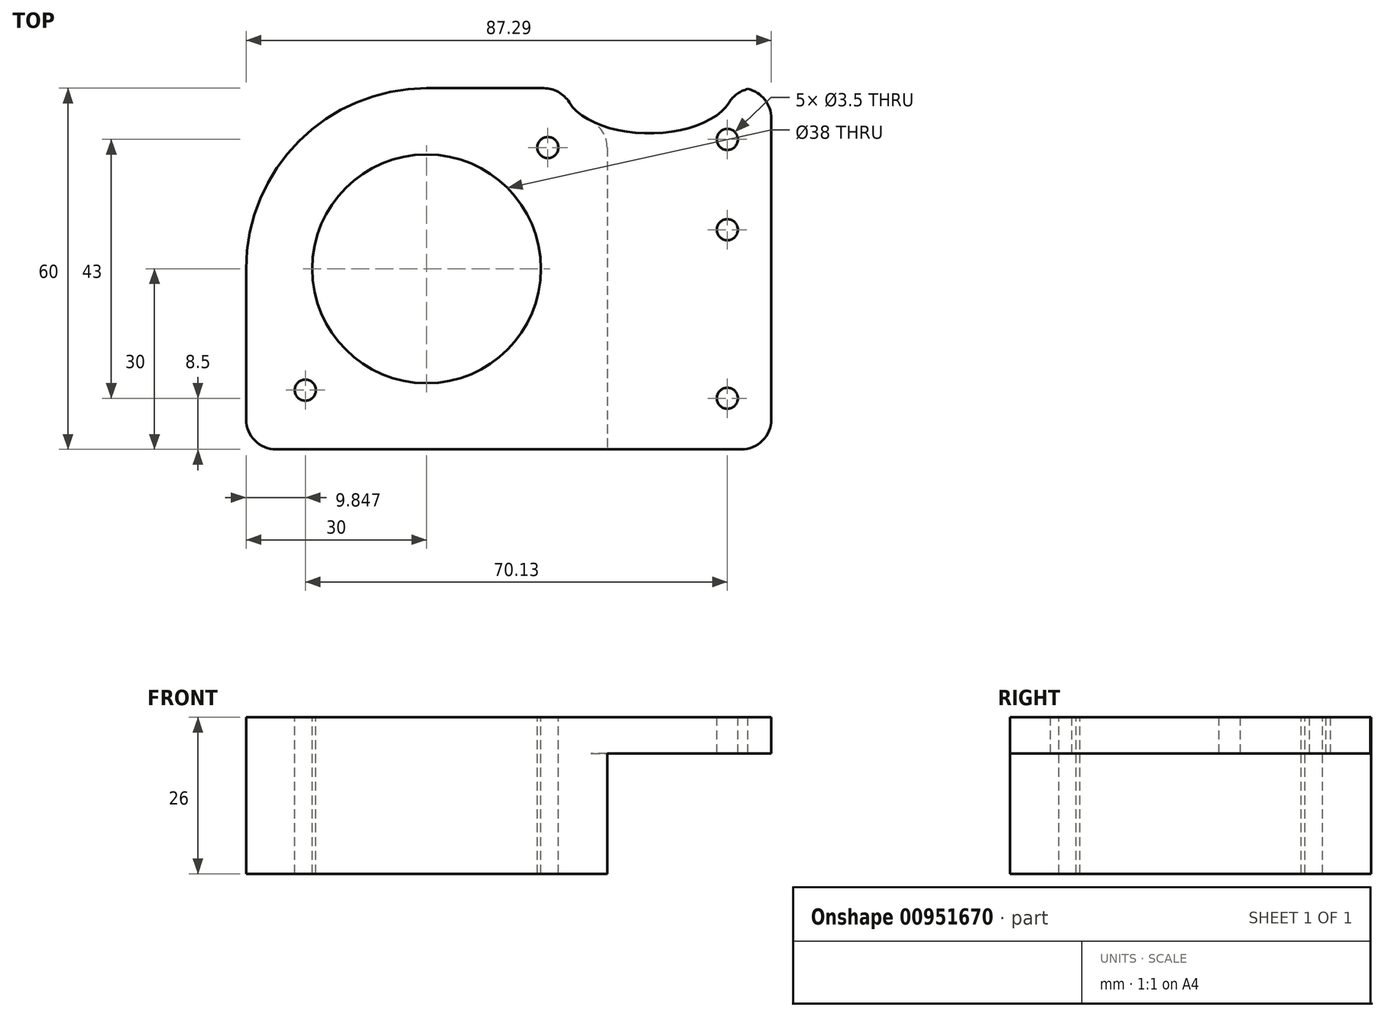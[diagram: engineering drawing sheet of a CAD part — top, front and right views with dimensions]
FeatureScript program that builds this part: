
annotation { "Feature Type Name" : "Feature", "Feature Type Description" : "" }
export const myFeature = defineFeature(function(context is Context, id is Id, definition is map)
    precondition{}
    {
        {
            var Q0;
            Q0=qCreatedBy(makeId("Top.planeOp"),FACE);
            var sketch = newSketch(context, id + "F0", { "sketchPlane" : qUnion([Q0])});
            skLineSegment(sketch, "E0.bottom", {"start": v(-68.25, 37.5) * mm, "end": v(68.25, 37.5) * mm});
            skLineSegment(sketch, "E0.top", {"start": v(-68.25, -37.5) * mm, "end": v(68.25, -37.5) * mm});
            skLineSegment(sketch, "E0.left", {"start": v(-68.25, 37.5) * mm, "end": v(-68.25, -37.5) * mm});
            skLineSegment(sketch, "E0.right", {"start": v(68.25, 37.5) * mm, "end": v(68.25, -37.5) * mm});
            skPoint(sketch, "E0.middle", {"position": v(0, 0) * mm});
            skCircle(sketch, "E1", {"center": v(-68.25, 37.5) * mm, "radius": 2.75 * mm});
            skCircle(sketch, "E2", {"center": v(68.25, 37.5) * mm, "radius": 2.75 * mm});
            skCircle(sketch, "E3", {"center": v(68.25, -37.5) * mm, "radius": 2.75 * mm});
            skCircle(sketch, "E4", {"center": v(-68.25, -37.5) * mm, "radius": 2.75 * mm});
            skEllipse(sketch, "E5", {"center": v(0, 37.5) * mm, "majorRadius": 6 * mm, "minorRadius": 2.75 * mm, "majorAxis": v(0, 1)});
            skEllipse(sketch, "E6", {"center": v(0, -37.5) * mm, "majorRadius": 6 * mm, "minorRadius": 2.75 * mm, "majorAxis": v(0, 1)});
            skLineSegment(sketch, "E7.bottom", {"start": v(-68.25, 37.5) * mm, "end": v(-75.25, 37.5) * mm});
            skLineSegment(sketch, "E7.top", {"start": v(-68.25, -37.5) * mm, "end": v(-75.25, -37.5) * mm});
            skLineSegment(sketch, "E7.right", {"start": v(-75.25, 37.5) * mm, "end": v(-75.25, -37.5) * mm});
            skLineSegment(sketch, "E8.bottom", {"start": v(-135.25, 37.5) * mm, "end": v(-75.25, 37.5) * mm});
            skLineSegment(sketch, "E8.top", {"start": v(-135.25, -22.5) * mm, "end": v(-75.25, -22.5) * mm});
            skLineSegment(sketch, "E8.left", {"start": v(-135.25, 37.5) * mm, "end": v(-135.25, -22.5) * mm});
            skLineSegment(sketch, "E8.right", {"start": v(-75.25, 30) * mm, "end": v(-75.25, -30) * mm});
            skPoint(sketch, "E8.middle", {"position": v(-75.25, 0) * mm});
            skCircle(sketch, "E9", {"center": v(-85.1, 27.65) * mm, "radius": 1.75 * mm});
            skCircle(sketch, "E10", {"center": v(-125.4, -12.65) * mm, "radius": 1.75 * mm});
            skCircle(sketch, "E11", {"center": v(-105.25, 7.5) * mm, "radius": 19 * mm});
            skCircle(sketch, "E12", {"center": v(-55.27, 29) * mm, "radius": 1.75 * mm});
            skCircle(sketch, "E13", {"center": v(-55.27, -14) * mm, "radius": 1.75 * mm});
            skCircle(sketch, "E14", {"center": v(-55.27, 14) * mm, "radius": 1.75 * mm});
            skEllipse(sketch, "E15", {"center": v(-68.25, 37.5) * mm, "majorRadius": 14 * mm, "minorRadius": 7.5 * mm, "majorAxis": v(-1, 0)});
            skLineSegment(sketch, "E16", {"start": v(-47.96, 37.5) * mm, "end": v(-47.96, -37.5) * mm});
            skLineSegment(sketch, "E17", {"start": v(-75.25, -22.5) * mm, "end": v(-47.96, -22.5) * mm});
            skArc(sketch, "E18", {"start": v(-105.25, 37.5) * mm, "mid": v(-126.46, 28.71) * mm, "end": v(-135.25, 7.5) * mm});
            skSolve(sketch);
        }
        {
            var Q0;
            Q0=makeQuery(id+"F0.imprint","IMPRINT",FACE,{"disambiguationData":[TD([[makeQuery(id+"F0.imprint","IMPRINT",EDGE,{"derivedFrom":sQuery(id+"F0.wireOp",EDGE,"E12")}),-1.0]])]});
            var Q1;
            {var subQ0=sQuery(id+"F0.wireOp",EDGE,"E15");var subQ1=sQuery(id+"F0.wireOp",EDGE,"E0.left");var subQ2=makeQuery(id+"F0.imprint","INTERSECT",VERTEX,{"derivedFrom":[subQ1,subQ0]});Q1=makeQuery(id+"F0.imprint","IMPRINT",FACE,{"disambiguationData":[TD([[makeQuery(id+"F0.imprint","IMPRINT",EDGE,{"disambiguationData":[TD([[subQ2,-1.0]])],"derivedFrom":subQ1}),-1.0]])]});}
            extrude(context, id + "F1", {"entities" : qUnion([Q0, Q1]), "oppositeDirection" : true, "depth" : 6 * mm, "offsetDistance" : 25 * mm});
        }
        {
            var Q0;
            {var subQ0=sQuery(id+"F0.wireOp",EDGE,"E8.top");Q0=makeQuery(id+"F0.imprint","IMPRINT",FACE,{"disambiguationData":[TD([[makeQuery(id+"F0.imprint","IMPRINT",EDGE,{"derivedFrom":subQ0}),1.0]])]});}
            extrude(context, id + "F2", {"entities" : qUnion([Q0]), "operationType" : NewBodyOperationType.ADD, "depth" : -26 * mm, "offsetDistance" : 25 * mm});
        }
        {
            var Q0;
            Q0=makeQuery(id+"F2.opExtrude","SWEPT_EDGE",EDGE,{"disambiguationData":[OSD([sQuery(id+"F0.wireOp",EDGE,"E8.bottom"),sQuery(id+"F0.wireOp",EDGE,"E8.left")])]});
            var Q1;
            Q1=makeQuery(id+"F2.opExtrude","SWEPT_EDGE",EDGE,{"disambiguationData":[OSD([sQuery(id+"F0.wireOp",EDGE,"E8.top"),sQuery(id+"F0.wireOp",EDGE,"E8.left")])]});
            var Q2;
            Q2=makeQuery(id+"F2.opExtrude","SWEPT_EDGE",EDGE,{"disambiguationData":[OSD([sQuery(id+"F0.wireOp",EDGE,"E7.bottom"),sQuery(id+"F0.wireOp",EDGE,"E7.right"),sQuery(id+"F0.wireOp",EDGE,"E8.bottom")])]});
            var Q3;
            {var subQ0=sQuery(id+"F0.wireOp",EDGE,"E8.right");var subQ1=sQuery(id+"F0.wireOp",EDGE,"E8.top");Q3=makeQuery(id+"F2.boolean.opBoolean","SPLIT",EDGE,{"disambiguationData":[topologyDisambiguationEdgeConnected([makeQuery(id+"F2.opExtrude","SWEPT_FACE",FACE,{"disambiguationData":[OSD([sQuery(id+"F0.wireOp",EDGE,"E7.right"),subQ0])]})])],"derivedFrom":makeQuery(id+"F2.opExtrude","SWEPT_EDGE",EDGE,{"disambiguationData":[OSD([subQ1,subQ0])]})});}
            var Q4;
            Q4=makeQuery(id+"F1.opExtrude","SWEPT_EDGE",EDGE,{"disambiguationData":[OSD([sQuery(id+"F0.wireOp",EDGE,"E7.top"),sQuery(id+"F0.wireOp",EDGE,"E7.right")])]});
            var Q5;
            Q5=makeQuery(id+"F1.opExtrude","SWEPT_EDGE",EDGE,{"disambiguationData":[OSD([sQuery(id+"F0.wireOp",EDGE,"E7.bottom"),sQuery(id+"F0.wireOp",EDGE,"E7.right"),sQuery(id+"F0.wireOp",EDGE,"E8.bottom")])]});
            var Q6;
            Q6=makeQuery(id+"F1.opExtrude","SWEPT_EDGE",EDGE,{"disambiguationData":[OSD([sQuery(id+"F0.wireOp",EDGE,"E0.bottom"),sQuery(id+"F0.wireOp",EDGE,"E15")])]});
            var Q7;
            Q7=makeQuery(id+"F1.opExtrude","SWEPT_EDGE",EDGE,{"disambiguationData":[OSD([sQuery(id+"F0.wireOp",EDGE,"E0.bottom"),sQuery(id+"F0.wireOp",EDGE,"E16")])]});
            var Q8;
            Q8=makeQuery(id+"F1.opExtrude","SWEPT_EDGE",EDGE,{"disambiguationData":[OSD([sQuery(id+"F0.wireOp",EDGE,"E16"),sQuery(id+"F0.wireOp",EDGE,"E17")])]});
            fillet(context, id + "F3", {"entities" : qUnion([Q0, Q1, Q2, Q3, Q4, Q5, Q6, Q7, Q8]), "radius" : 5 * mm, "tangentPropagation" : true, "allowEdgeOverflow" : false});
        }
    });
